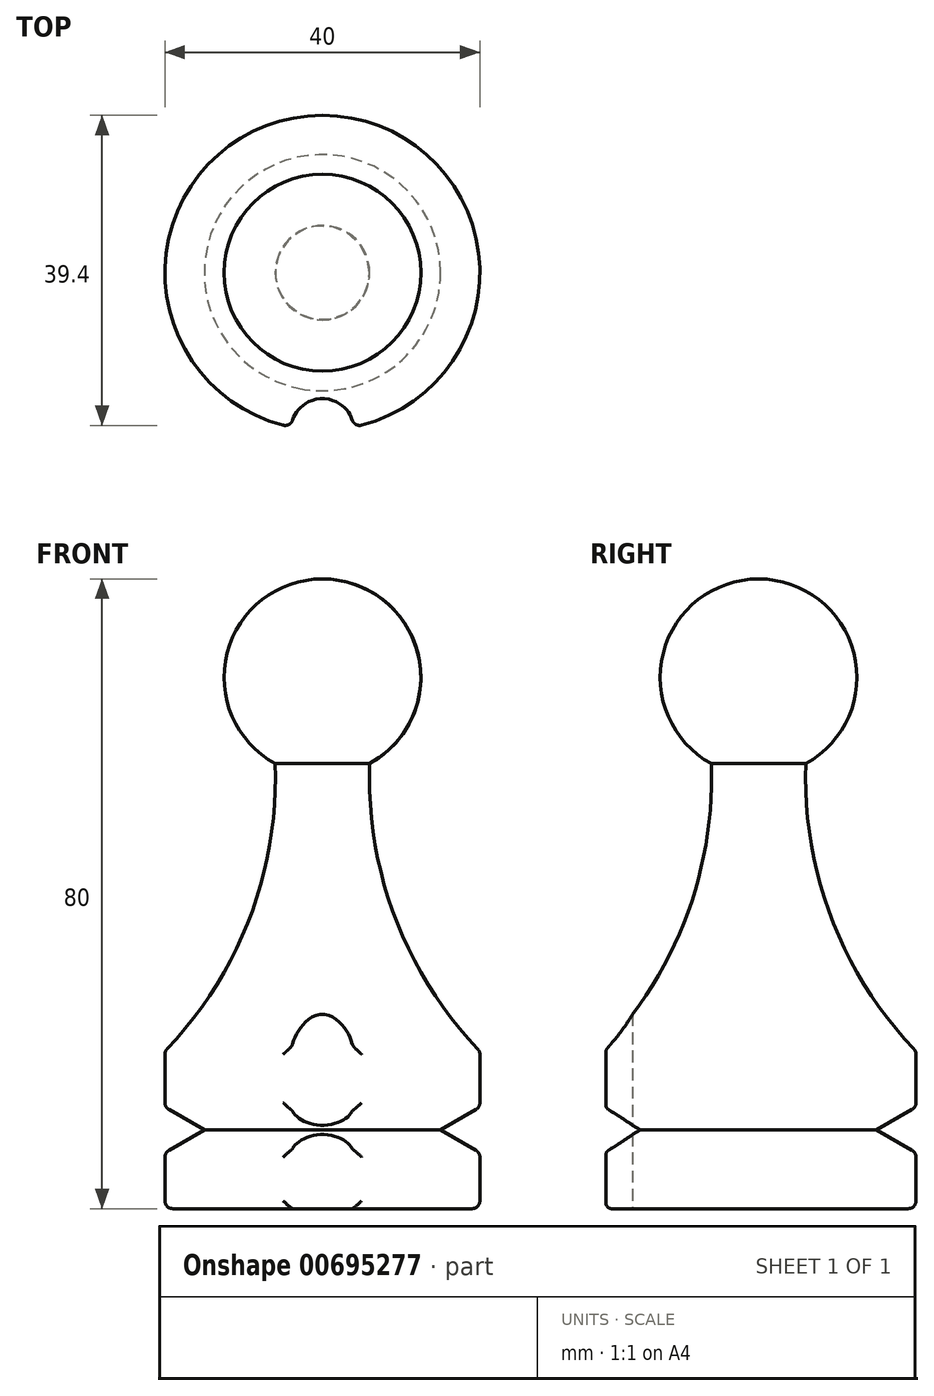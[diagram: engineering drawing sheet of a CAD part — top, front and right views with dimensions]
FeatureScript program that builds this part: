
annotation { "Feature Type Name" : "Feature", "Feature Type Description" : "" }
export const myFeature = defineFeature(function(context is Context, id is Id, definition is map)
    precondition{}
    {
        {
            var Q0;
            Q0=qCreatedBy(makeId("Front.planeOp"),FACE);
            var sketch = newSketch(context, id + "F0", { "sketchPlane" : qUnion([Q0])});
            skLineSegment(sketch, "E0", {"start": v(0, 87.13) * mm, "end": v(0, -76.3) * mm, "construction": true});
            skLineSegment(sketch, "E1", {"start": v(0, 0) * mm, "end": v(20, 0) * mm});
            skLineSegment(sketch, "E2", {"start": v(20, 0) * mm, "end": v(20, 7.11) * mm});
            skArc(sketch, "E3", {"start": v(6, 56.53) * mm, "mid": v(9.28, 36.84) * mm, "end": v(20, 20) * mm});
            skArc(sketch, "E4", {"start": v(6, 56.53) * mm, "mid": v(12.11, 70.6) * mm, "end": v(0, 80) * mm});
            skLineSegment(sketch, "E5", {"start": v(15, 10) * mm, "end": v(20, 7.11) * mm});
            skPoint(sketch, "E5.startSnap0", {"position": v(20, 10) * mm});
            skLineSegment(sketch, "E6", {"start": v(20, 7.11) * mm, "end": v(15, 10) * mm});
            skLineSegment(sketch, "E7", {"start": v(15, 10) * mm, "end": v(20, 12.89) * mm});
            skLineSegment(sketch, "E8.trimOffspring", {"start": v(20, 12.89) * mm, "end": v(20, 20) * mm});
            skLineSegment(sketch, "E9", {"start": v(0, 80) * mm, "end": v(0, 0) * mm});
            skSolve(sketch);
        }
        {
            var Q0;
            Q0 = qSketchRegion(id + "F0", true);
            var Q1;
            Q1=sQuery(id+"F0.wireOp",EDGE,"E0");
            revolve(context, id + "F1", {"entities" : qUnion([Q0]), "axis" : qUnion([Q1]), "revolveType" : RevolveType.FULL});
        }
        {
            var Q0;
            Q0=qCreatedBy(makeId("Top.planeOp"),FACE);
            var sketch = newSketch(context, id + "F2", { "sketchPlane" : qUnion([Q0])});
            skCircle(sketch, "E10.0", {"center": v(0, 0) * mm, "radius": 20 * mm});
            skCircle(sketch, "E11", {"center": v(0, -20) * mm, "radius": 4 * mm});
            skSolve(sketch);
        }
        {
            var Q0;
            {var subQ0=sQuery(id+"F2.wireOp",EDGE,"E11");var subQ1=sQuery(id+"F2.wireOp",EDGE,"E10.0");var subQ2=makeQuery(id+"F2.imprint","INTERSECT",VERTEX,{"disambiguationData":[OD(0.0)],"derivedFrom":[subQ1,subQ0]});Q0=makeQuery(id+"F2.imprint","IMPRINT",FACE,{"disambiguationData":[TD([[makeQuery(id+"F2.imprint","IMPRINT",EDGE,{"disambiguationData":[TD([[subQ2,-1.0]])],"derivedFrom":subQ1}),1.0]])]});}
            extrude(context, id + "F3", {"entities" : qUnion([Q0]), "operationType" : NewBodyOperationType.REMOVE, "depth" : 36.6 * mm, "offsetDistance" : 25 * mm});
        }
        {
            var Q0;
            {var subQ0=makeQuery(id+"F1.opRevolve","SWEPT_FACE",FACE,{"disambiguationData":[OSD([sQuery(id+"F0.wireOp",EDGE,"E3")])]});var subQ2=makeQuery(id+"F1.opRevolve","SWEPT_FACE",FACE,{"disambiguationData":[OSD([sQuery(id+"F0.wireOp",EDGE,"E8.trimOffspring")])]});var subQ3=sQuery(id+"F2.wireOp",EDGE,"E11");var subQ4=makeQuery(id+"F3.boolean.opBoolean","COPY",FACE,{"disambiguationData":[TD([subQ0])],"derivedFrom":makeQuery(id+"F3.opExtrude","SWEPT_FACE",FACE,{"disambiguationData":[OSD([subQ3])]})});Q0=makeQuery(id+"FiWPijupLubemqV_1.9.F3.boolean.opBoolean","SPLIT",FACE,{"disambiguationData":[TD([subQ4])],"derivedFrom":makeQuery(id+"FiWPijupLubemqV_1.8.F3.boolean.opBoolean","SPLIT",FACE,{"disambiguationData":[TD([subQ4])],"derivedFrom":makeQuery(id+"FiWPijupLubemqV_1.7.F3.boolean.opBoolean","SPLIT",FACE,{"disambiguationData":[TD([subQ4])],"derivedFrom":makeQuery(id+"FiWPijupLubemqV_1.6.F3.boolean.opBoolean","SPLIT",FACE,{"disambiguationData":[TD([subQ4])],"derivedFrom":makeQuery(id+"FiWPijupLubemqV_1.5.F3.boolean.opBoolean","SPLIT",FACE,{"disambiguationData":[TD([subQ4])],"derivedFrom":makeQuery(id+"FiWPijupLubemqV_1.4.F3.boolean.opBoolean","SPLIT",FACE,{"disambiguationData":[TD([subQ4])],"derivedFrom":makeQuery(id+"FiWPijupLubemqV_1.3.F3.boolean.opBoolean","SPLIT",FACE,{"disambiguationData":[TD([subQ4])],"derivedFrom":makeQuery(id+"FiWPijupLubemqV_1.2.F3.boolean.opBoolean","SPLIT",FACE,{"disambiguationData":[TD([subQ4])],"derivedFrom":makeQuery(id+"FiWPijupLubemqV_1.1.F3.boolean.opBoolean","SPLIT",FACE,{"disambiguationData":[OD(1.0)],"derivedFrom":subQ2})})})})})})})})});}
            var Q1;
            {var subQ0=makeQuery(id+"F1.opRevolve","SWEPT_FACE",FACE,{"disambiguationData":[OSD([sQuery(id+"F0.wireOp",EDGE,"E3")])]});var subQ2=makeQuery(id+"F1.opRevolve","SWEPT_FACE",FACE,{"disambiguationData":[OSD([sQuery(id+"F0.wireOp",EDGE,"E8.trimOffspring")])]});var subQ3=sQuery(id+"F2.wireOp",EDGE,"E11");var subQ4=makeQuery(id+"FiWPijupLubemqV_1.8.F3.opExtrude","SWEPT_FACE",FACE,{"disambiguationData":[OSD([subQ3])]});var subQ5=makeQuery(id+"F3.boolean.opBoolean","COPY",FACE,{"disambiguationData":[TD([subQ0])],"derivedFrom":makeQuery(id+"F3.opExtrude","SWEPT_FACE",FACE,{"disambiguationData":[OSD([subQ3])]})});Q1=makeQuery(id+"FiWPijupLubemqV_1.9.F3.boolean.opBoolean","SPLIT",FACE,{"disambiguationData":[TD([makeQuery(id+"FiWPijupLubemqV_1.8.F3.boolean.opBoolean","COPY",FACE,{"disambiguationData":[TD([subQ0])],"derivedFrom":subQ4})])],"derivedFrom":makeQuery(id+"FiWPijupLubemqV_1.8.F3.boolean.opBoolean","SPLIT",FACE,{"disambiguationData":[TD([subQ5])],"derivedFrom":makeQuery(id+"FiWPijupLubemqV_1.7.F3.boolean.opBoolean","SPLIT",FACE,{"disambiguationData":[TD([subQ5])],"derivedFrom":makeQuery(id+"FiWPijupLubemqV_1.6.F3.boolean.opBoolean","SPLIT",FACE,{"disambiguationData":[TD([subQ5])],"derivedFrom":makeQuery(id+"FiWPijupLubemqV_1.5.F3.boolean.opBoolean","SPLIT",FACE,{"disambiguationData":[TD([subQ5])],"derivedFrom":makeQuery(id+"FiWPijupLubemqV_1.4.F3.boolean.opBoolean","SPLIT",FACE,{"disambiguationData":[TD([subQ5])],"derivedFrom":makeQuery(id+"FiWPijupLubemqV_1.3.F3.boolean.opBoolean","SPLIT",FACE,{"disambiguationData":[TD([subQ5])],"derivedFrom":makeQuery(id+"FiWPijupLubemqV_1.2.F3.boolean.opBoolean","SPLIT",FACE,{"disambiguationData":[TD([subQ5])],"derivedFrom":makeQuery(id+"FiWPijupLubemqV_1.1.F3.boolean.opBoolean","SPLIT",FACE,{"disambiguationData":[OD(1.0)],"derivedFrom":subQ2})})})})})})})})});}
            var Q2;
            Q2=makeQuery(id+"FiWPijupLubemqV_1.1.F3.boolean.opBoolean","SPLIT",FACE,{"disambiguationData":[OD(0.0)],"derivedFrom":makeQuery(id+"F1.opRevolve","SWEPT_FACE",FACE,{"disambiguationData":[OSD([sQuery(id+"F0.wireOp",EDGE,"E8.trimOffspring")])]})});
            var Q3;
            {var subQ0=makeQuery(id+"F1.opRevolve","SWEPT_FACE",FACE,{"disambiguationData":[OSD([sQuery(id+"F0.wireOp",EDGE,"E3")])]});var subQ2=makeQuery(id+"F1.opRevolve","SWEPT_FACE",FACE,{"disambiguationData":[OSD([sQuery(id+"F0.wireOp",EDGE,"E8.trimOffspring")])]});var subQ3=sQuery(id+"F2.wireOp",EDGE,"E11");Q3=makeQuery(id+"FiWPijupLubemqV_1.2.F3.boolean.opBoolean","SPLIT",FACE,{"disambiguationData":[TD([makeQuery(id+"FiWPijupLubemqV_1.1.F3.boolean.opBoolean","COPY",FACE,{"disambiguationData":[TD([subQ0])],"derivedFrom":makeQuery(id+"FiWPijupLubemqV_1.1.F3.opExtrude","SWEPT_FACE",FACE,{"disambiguationData":[OSD([subQ3])]})})])],"derivedFrom":makeQuery(id+"FiWPijupLubemqV_1.1.F3.boolean.opBoolean","SPLIT",FACE,{"disambiguationData":[OD(1.0)],"derivedFrom":subQ2})});}
            var Q4;
            {var subQ0=makeQuery(id+"F1.opRevolve","SWEPT_FACE",FACE,{"disambiguationData":[OSD([sQuery(id+"F0.wireOp",EDGE,"E3")])]});var subQ2=makeQuery(id+"F1.opRevolve","SWEPT_FACE",FACE,{"disambiguationData":[OSD([sQuery(id+"F0.wireOp",EDGE,"E8.trimOffspring")])]});var subQ3=sQuery(id+"F2.wireOp",EDGE,"E11");var subQ4=makeQuery(id+"FiWPijupLubemqV_1.2.F3.opExtrude","SWEPT_FACE",FACE,{"disambiguationData":[OSD([subQ3])]});Q4=makeQuery(id+"FiWPijupLubemqV_1.3.F3.boolean.opBoolean","SPLIT",FACE,{"disambiguationData":[TD([makeQuery(id+"FiWPijupLubemqV_1.2.F3.boolean.opBoolean","COPY",FACE,{"disambiguationData":[TD([subQ0])],"derivedFrom":subQ4})])],"derivedFrom":makeQuery(id+"FiWPijupLubemqV_1.2.F3.boolean.opBoolean","SPLIT",FACE,{"disambiguationData":[TD([makeQuery(id+"F3.boolean.opBoolean","COPY",FACE,{"disambiguationData":[TD([subQ0])],"derivedFrom":makeQuery(id+"F3.opExtrude","SWEPT_FACE",FACE,{"disambiguationData":[OSD([subQ3])]})})])],"derivedFrom":makeQuery(id+"FiWPijupLubemqV_1.1.F3.boolean.opBoolean","SPLIT",FACE,{"disambiguationData":[OD(1.0)],"derivedFrom":subQ2})})});}
            var Q5;
            {var subQ0=makeQuery(id+"F1.opRevolve","SWEPT_FACE",FACE,{"disambiguationData":[OSD([sQuery(id+"F0.wireOp",EDGE,"E3")])]});var subQ2=makeQuery(id+"F1.opRevolve","SWEPT_FACE",FACE,{"disambiguationData":[OSD([sQuery(id+"F0.wireOp",EDGE,"E8.trimOffspring")])]});var subQ3=sQuery(id+"F2.wireOp",EDGE,"E11");var subQ4=makeQuery(id+"FiWPijupLubemqV_1.3.F3.opExtrude","SWEPT_FACE",FACE,{"disambiguationData":[OSD([subQ3])]});var subQ5=makeQuery(id+"F3.boolean.opBoolean","COPY",FACE,{"disambiguationData":[TD([subQ0])],"derivedFrom":makeQuery(id+"F3.opExtrude","SWEPT_FACE",FACE,{"disambiguationData":[OSD([subQ3])]})});Q5=makeQuery(id+"FiWPijupLubemqV_1.4.F3.boolean.opBoolean","SPLIT",FACE,{"disambiguationData":[TD([makeQuery(id+"FiWPijupLubemqV_1.3.F3.boolean.opBoolean","COPY",FACE,{"disambiguationData":[TD([subQ0])],"derivedFrom":subQ4})])],"derivedFrom":makeQuery(id+"FiWPijupLubemqV_1.3.F3.boolean.opBoolean","SPLIT",FACE,{"disambiguationData":[TD([subQ5])],"derivedFrom":makeQuery(id+"FiWPijupLubemqV_1.2.F3.boolean.opBoolean","SPLIT",FACE,{"disambiguationData":[TD([subQ5])],"derivedFrom":makeQuery(id+"FiWPijupLubemqV_1.1.F3.boolean.opBoolean","SPLIT",FACE,{"disambiguationData":[OD(1.0)],"derivedFrom":subQ2})})})});}
            var Q6;
            {var subQ0=makeQuery(id+"F1.opRevolve","SWEPT_FACE",FACE,{"disambiguationData":[OSD([sQuery(id+"F0.wireOp",EDGE,"E3")])]});var subQ2=makeQuery(id+"F1.opRevolve","SWEPT_FACE",FACE,{"disambiguationData":[OSD([sQuery(id+"F0.wireOp",EDGE,"E8.trimOffspring")])]});var subQ3=sQuery(id+"F2.wireOp",EDGE,"E11");var subQ4=makeQuery(id+"FiWPijupLubemqV_1.4.F3.opExtrude","SWEPT_FACE",FACE,{"disambiguationData":[OSD([subQ3])]});var subQ5=makeQuery(id+"F3.boolean.opBoolean","COPY",FACE,{"disambiguationData":[TD([subQ0])],"derivedFrom":makeQuery(id+"F3.opExtrude","SWEPT_FACE",FACE,{"disambiguationData":[OSD([subQ3])]})});Q6=makeQuery(id+"FiWPijupLubemqV_1.5.F3.boolean.opBoolean","SPLIT",FACE,{"disambiguationData":[TD([makeQuery(id+"FiWPijupLubemqV_1.4.F3.boolean.opBoolean","COPY",FACE,{"disambiguationData":[TD([subQ0])],"derivedFrom":subQ4})])],"derivedFrom":makeQuery(id+"FiWPijupLubemqV_1.4.F3.boolean.opBoolean","SPLIT",FACE,{"disambiguationData":[TD([subQ5])],"derivedFrom":makeQuery(id+"FiWPijupLubemqV_1.3.F3.boolean.opBoolean","SPLIT",FACE,{"disambiguationData":[TD([subQ5])],"derivedFrom":makeQuery(id+"FiWPijupLubemqV_1.2.F3.boolean.opBoolean","SPLIT",FACE,{"disambiguationData":[TD([subQ5])],"derivedFrom":makeQuery(id+"FiWPijupLubemqV_1.1.F3.boolean.opBoolean","SPLIT",FACE,{"disambiguationData":[OD(1.0)],"derivedFrom":subQ2})})})})});}
            var Q7;
            {var subQ0=makeQuery(id+"F1.opRevolve","SWEPT_FACE",FACE,{"disambiguationData":[OSD([sQuery(id+"F0.wireOp",EDGE,"E3")])]});var subQ2=makeQuery(id+"F1.opRevolve","SWEPT_FACE",FACE,{"disambiguationData":[OSD([sQuery(id+"F0.wireOp",EDGE,"E8.trimOffspring")])]});var subQ3=sQuery(id+"F2.wireOp",EDGE,"E11");var subQ4=makeQuery(id+"FiWPijupLubemqV_1.5.F3.opExtrude","SWEPT_FACE",FACE,{"disambiguationData":[OSD([subQ3])]});var subQ5=makeQuery(id+"F3.boolean.opBoolean","COPY",FACE,{"disambiguationData":[TD([subQ0])],"derivedFrom":makeQuery(id+"F3.opExtrude","SWEPT_FACE",FACE,{"disambiguationData":[OSD([subQ3])]})});Q7=makeQuery(id+"FiWPijupLubemqV_1.6.F3.boolean.opBoolean","SPLIT",FACE,{"disambiguationData":[TD([makeQuery(id+"FiWPijupLubemqV_1.5.F3.boolean.opBoolean","COPY",FACE,{"disambiguationData":[TD([subQ0])],"derivedFrom":subQ4})])],"derivedFrom":makeQuery(id+"FiWPijupLubemqV_1.5.F3.boolean.opBoolean","SPLIT",FACE,{"disambiguationData":[TD([subQ5])],"derivedFrom":makeQuery(id+"FiWPijupLubemqV_1.4.F3.boolean.opBoolean","SPLIT",FACE,{"disambiguationData":[TD([subQ5])],"derivedFrom":makeQuery(id+"FiWPijupLubemqV_1.3.F3.boolean.opBoolean","SPLIT",FACE,{"disambiguationData":[TD([subQ5])],"derivedFrom":makeQuery(id+"FiWPijupLubemqV_1.2.F3.boolean.opBoolean","SPLIT",FACE,{"disambiguationData":[TD([subQ5])],"derivedFrom":makeQuery(id+"FiWPijupLubemqV_1.1.F3.boolean.opBoolean","SPLIT",FACE,{"disambiguationData":[OD(1.0)],"derivedFrom":subQ2})})})})})});}
            var Q8;
            {var subQ0=makeQuery(id+"F1.opRevolve","SWEPT_FACE",FACE,{"disambiguationData":[OSD([sQuery(id+"F0.wireOp",EDGE,"E3")])]});var subQ2=makeQuery(id+"F1.opRevolve","SWEPT_FACE",FACE,{"disambiguationData":[OSD([sQuery(id+"F0.wireOp",EDGE,"E8.trimOffspring")])]});var subQ3=sQuery(id+"F2.wireOp",EDGE,"E11");var subQ4=makeQuery(id+"FiWPijupLubemqV_1.7.F3.opExtrude","SWEPT_FACE",FACE,{"disambiguationData":[OSD([subQ3])]});var subQ5=makeQuery(id+"F3.boolean.opBoolean","COPY",FACE,{"disambiguationData":[TD([subQ0])],"derivedFrom":makeQuery(id+"F3.opExtrude","SWEPT_FACE",FACE,{"disambiguationData":[OSD([subQ3])]})});Q8=makeQuery(id+"FiWPijupLubemqV_1.8.F3.boolean.opBoolean","SPLIT",FACE,{"disambiguationData":[TD([makeQuery(id+"FiWPijupLubemqV_1.7.F3.boolean.opBoolean","COPY",FACE,{"disambiguationData":[TD([subQ0])],"derivedFrom":subQ4})])],"derivedFrom":makeQuery(id+"FiWPijupLubemqV_1.7.F3.boolean.opBoolean","SPLIT",FACE,{"disambiguationData":[TD([subQ5])],"derivedFrom":makeQuery(id+"FiWPijupLubemqV_1.6.F3.boolean.opBoolean","SPLIT",FACE,{"disambiguationData":[TD([subQ5])],"derivedFrom":makeQuery(id+"FiWPijupLubemqV_1.5.F3.boolean.opBoolean","SPLIT",FACE,{"disambiguationData":[TD([subQ5])],"derivedFrom":makeQuery(id+"FiWPijupLubemqV_1.4.F3.boolean.opBoolean","SPLIT",FACE,{"disambiguationData":[TD([subQ5])],"derivedFrom":makeQuery(id+"FiWPijupLubemqV_1.3.F3.boolean.opBoolean","SPLIT",FACE,{"disambiguationData":[TD([subQ5])],"derivedFrom":makeQuery(id+"FiWPijupLubemqV_1.2.F3.boolean.opBoolean","SPLIT",FACE,{"disambiguationData":[TD([subQ5])],"derivedFrom":makeQuery(id+"FiWPijupLubemqV_1.1.F3.boolean.opBoolean","SPLIT",FACE,{"disambiguationData":[OD(1.0)],"derivedFrom":subQ2})})})})})})})});}
            var Q9;
            {var subQ0=makeQuery(id+"F1.opRevolve","SWEPT_FACE",FACE,{"disambiguationData":[OSD([sQuery(id+"F0.wireOp",EDGE,"E3")])]});var subQ2=makeQuery(id+"F1.opRevolve","SWEPT_FACE",FACE,{"disambiguationData":[OSD([sQuery(id+"F0.wireOp",EDGE,"E8.trimOffspring")])]});var subQ3=sQuery(id+"F2.wireOp",EDGE,"E11");var subQ4=makeQuery(id+"FiWPijupLubemqV_1.6.F3.opExtrude","SWEPT_FACE",FACE,{"disambiguationData":[OSD([subQ3])]});var subQ5=makeQuery(id+"F3.boolean.opBoolean","COPY",FACE,{"disambiguationData":[TD([subQ0])],"derivedFrom":makeQuery(id+"F3.opExtrude","SWEPT_FACE",FACE,{"disambiguationData":[OSD([subQ3])]})});Q9=makeQuery(id+"FiWPijupLubemqV_1.7.F3.boolean.opBoolean","SPLIT",FACE,{"disambiguationData":[TD([makeQuery(id+"FiWPijupLubemqV_1.6.F3.boolean.opBoolean","COPY",FACE,{"disambiguationData":[TD([subQ0])],"derivedFrom":subQ4})])],"derivedFrom":makeQuery(id+"FiWPijupLubemqV_1.6.F3.boolean.opBoolean","SPLIT",FACE,{"disambiguationData":[TD([subQ5])],"derivedFrom":makeQuery(id+"FiWPijupLubemqV_1.5.F3.boolean.opBoolean","SPLIT",FACE,{"disambiguationData":[TD([subQ5])],"derivedFrom":makeQuery(id+"FiWPijupLubemqV_1.4.F3.boolean.opBoolean","SPLIT",FACE,{"disambiguationData":[TD([subQ5])],"derivedFrom":makeQuery(id+"FiWPijupLubemqV_1.3.F3.boolean.opBoolean","SPLIT",FACE,{"disambiguationData":[TD([subQ5])],"derivedFrom":makeQuery(id+"FiWPijupLubemqV_1.2.F3.boolean.opBoolean","SPLIT",FACE,{"disambiguationData":[TD([subQ5])],"derivedFrom":makeQuery(id+"FiWPijupLubemqV_1.1.F3.boolean.opBoolean","SPLIT",FACE,{"disambiguationData":[OD(1.0)],"derivedFrom":subQ2})})})})})})});}
            var Q10;
            {var subQ0=makeQuery(id+"F1.opRevolve","SWEPT_FACE",FACE,{"disambiguationData":[OSD([sQuery(id+"F0.wireOp",EDGE,"E1")])]});var subQ2=makeQuery(id+"F1.opRevolve","SWEPT_FACE",FACE,{"disambiguationData":[OSD([sQuery(id+"F0.wireOp",EDGE,"E2")])]});var subQ3=sQuery(id+"F2.wireOp",EDGE,"E11");var subQ4=makeQuery(id+"FiWPijupLubemqV_1.7.F3.opExtrude","SWEPT_FACE",FACE,{"disambiguationData":[OSD([subQ3])]});var subQ5=makeQuery(id+"F3.boolean.opBoolean","COPY",FACE,{"disambiguationData":[TD([subQ0])],"derivedFrom":makeQuery(id+"F3.opExtrude","SWEPT_FACE",FACE,{"disambiguationData":[OSD([subQ3])]})});Q10=makeQuery(id+"FiWPijupLubemqV_1.8.F3.boolean.opBoolean","SPLIT",FACE,{"disambiguationData":[TD([makeQuery(id+"FiWPijupLubemqV_1.7.F3.boolean.opBoolean","COPY",FACE,{"disambiguationData":[TD([subQ0])],"derivedFrom":subQ4})])],"derivedFrom":makeQuery(id+"FiWPijupLubemqV_1.7.F3.boolean.opBoolean","SPLIT",FACE,{"disambiguationData":[TD([subQ5])],"derivedFrom":makeQuery(id+"FiWPijupLubemqV_1.6.F3.boolean.opBoolean","SPLIT",FACE,{"disambiguationData":[TD([subQ5])],"derivedFrom":makeQuery(id+"FiWPijupLubemqV_1.5.F3.boolean.opBoolean","SPLIT",FACE,{"disambiguationData":[TD([subQ5])],"derivedFrom":makeQuery(id+"FiWPijupLubemqV_1.4.F3.boolean.opBoolean","SPLIT",FACE,{"disambiguationData":[TD([subQ5])],"derivedFrom":makeQuery(id+"FiWPijupLubemqV_1.3.F3.boolean.opBoolean","SPLIT",FACE,{"disambiguationData":[TD([subQ5])],"derivedFrom":makeQuery(id+"FiWPijupLubemqV_1.2.F3.boolean.opBoolean","SPLIT",FACE,{"disambiguationData":[TD([subQ5])],"derivedFrom":makeQuery(id+"FiWPijupLubemqV_1.1.F3.boolean.opBoolean","SPLIT",FACE,{"disambiguationData":[OD(1.0)],"derivedFrom":subQ2})})})})})})})});}
            var Q11;
            {var subQ0=makeQuery(id+"F1.opRevolve","SWEPT_FACE",FACE,{"disambiguationData":[OSD([sQuery(id+"F0.wireOp",EDGE,"E1")])]});var subQ1=sQuery(id+"F2.wireOp",EDGE,"E11");var subQ3=makeQuery(id+"F1.opRevolve","SWEPT_FACE",FACE,{"disambiguationData":[OSD([sQuery(id+"F0.wireOp",EDGE,"E2")])]});var subQ4=makeQuery(id+"FiWPijupLubemqV_1.6.F3.opExtrude","SWEPT_FACE",FACE,{"disambiguationData":[OSD([subQ1])]});var subQ5=makeQuery(id+"F3.boolean.opBoolean","COPY",FACE,{"disambiguationData":[TD([subQ0])],"derivedFrom":makeQuery(id+"F3.opExtrude","SWEPT_FACE",FACE,{"disambiguationData":[OSD([subQ1])]})});Q11=makeQuery(id+"FiWPijupLubemqV_1.7.F3.boolean.opBoolean","SPLIT",FACE,{"disambiguationData":[TD([makeQuery(id+"FiWPijupLubemqV_1.6.F3.boolean.opBoolean","COPY",FACE,{"disambiguationData":[TD([subQ0])],"derivedFrom":subQ4})])],"derivedFrom":makeQuery(id+"FiWPijupLubemqV_1.6.F3.boolean.opBoolean","SPLIT",FACE,{"disambiguationData":[TD([subQ5])],"derivedFrom":makeQuery(id+"FiWPijupLubemqV_1.5.F3.boolean.opBoolean","SPLIT",FACE,{"disambiguationData":[TD([subQ5])],"derivedFrom":makeQuery(id+"FiWPijupLubemqV_1.4.F3.boolean.opBoolean","SPLIT",FACE,{"disambiguationData":[TD([subQ5])],"derivedFrom":makeQuery(id+"FiWPijupLubemqV_1.3.F3.boolean.opBoolean","SPLIT",FACE,{"disambiguationData":[TD([subQ5])],"derivedFrom":makeQuery(id+"FiWPijupLubemqV_1.2.F3.boolean.opBoolean","SPLIT",FACE,{"disambiguationData":[TD([subQ5])],"derivedFrom":makeQuery(id+"FiWPijupLubemqV_1.1.F3.boolean.opBoolean","SPLIT",FACE,{"disambiguationData":[OD(1.0)],"derivedFrom":subQ3})})})})})})});}
            var Q12;
            {var subQ0=makeQuery(id+"F1.opRevolve","SWEPT_FACE",FACE,{"disambiguationData":[OSD([sQuery(id+"F0.wireOp",EDGE,"E1")])]});var subQ2=makeQuery(id+"F1.opRevolve","SWEPT_FACE",FACE,{"disambiguationData":[OSD([sQuery(id+"F0.wireOp",EDGE,"E2")])]});var subQ3=sQuery(id+"F2.wireOp",EDGE,"E11");var subQ4=makeQuery(id+"FiWPijupLubemqV_1.5.F3.opExtrude","SWEPT_FACE",FACE,{"disambiguationData":[OSD([subQ3])]});var subQ5=makeQuery(id+"F3.boolean.opBoolean","COPY",FACE,{"disambiguationData":[TD([subQ0])],"derivedFrom":makeQuery(id+"F3.opExtrude","SWEPT_FACE",FACE,{"disambiguationData":[OSD([subQ3])]})});Q12=makeQuery(id+"FiWPijupLubemqV_1.6.F3.boolean.opBoolean","SPLIT",FACE,{"disambiguationData":[TD([makeQuery(id+"FiWPijupLubemqV_1.5.F3.boolean.opBoolean","COPY",FACE,{"disambiguationData":[TD([subQ0])],"derivedFrom":subQ4})])],"derivedFrom":makeQuery(id+"FiWPijupLubemqV_1.5.F3.boolean.opBoolean","SPLIT",FACE,{"disambiguationData":[TD([subQ5])],"derivedFrom":makeQuery(id+"FiWPijupLubemqV_1.4.F3.boolean.opBoolean","SPLIT",FACE,{"disambiguationData":[TD([subQ5])],"derivedFrom":makeQuery(id+"FiWPijupLubemqV_1.3.F3.boolean.opBoolean","SPLIT",FACE,{"disambiguationData":[TD([subQ5])],"derivedFrom":makeQuery(id+"FiWPijupLubemqV_1.2.F3.boolean.opBoolean","SPLIT",FACE,{"disambiguationData":[TD([subQ5])],"derivedFrom":makeQuery(id+"FiWPijupLubemqV_1.1.F3.boolean.opBoolean","SPLIT",FACE,{"disambiguationData":[OD(1.0)],"derivedFrom":subQ2})})})})})});}
            var Q13;
            {var subQ0=makeQuery(id+"F1.opRevolve","SWEPT_FACE",FACE,{"disambiguationData":[OSD([sQuery(id+"F0.wireOp",EDGE,"E1")])]});var subQ1=makeQuery(id+"F1.opRevolve","SWEPT_FACE",FACE,{"disambiguationData":[OSD([sQuery(id+"F0.wireOp",EDGE,"E2")])]});var subQ3=sQuery(id+"F2.wireOp",EDGE,"E11");var subQ4=makeQuery(id+"FiWPijupLubemqV_1.4.F3.opExtrude","SWEPT_FACE",FACE,{"disambiguationData":[OSD([subQ3])]});var subQ5=makeQuery(id+"F3.boolean.opBoolean","COPY",FACE,{"disambiguationData":[TD([subQ0])],"derivedFrom":makeQuery(id+"F3.opExtrude","SWEPT_FACE",FACE,{"disambiguationData":[OSD([subQ3])]})});Q13=makeQuery(id+"FiWPijupLubemqV_1.5.F3.boolean.opBoolean","SPLIT",FACE,{"disambiguationData":[TD([makeQuery(id+"FiWPijupLubemqV_1.4.F3.boolean.opBoolean","COPY",FACE,{"disambiguationData":[TD([subQ0])],"derivedFrom":subQ4})])],"derivedFrom":makeQuery(id+"FiWPijupLubemqV_1.4.F3.boolean.opBoolean","SPLIT",FACE,{"disambiguationData":[TD([subQ5])],"derivedFrom":makeQuery(id+"FiWPijupLubemqV_1.3.F3.boolean.opBoolean","SPLIT",FACE,{"disambiguationData":[TD([subQ5])],"derivedFrom":makeQuery(id+"FiWPijupLubemqV_1.2.F3.boolean.opBoolean","SPLIT",FACE,{"disambiguationData":[TD([subQ5])],"derivedFrom":makeQuery(id+"FiWPijupLubemqV_1.1.F3.boolean.opBoolean","SPLIT",FACE,{"disambiguationData":[OD(1.0)],"derivedFrom":subQ1})})})})});}
            var Q14;
            {var subQ0=makeQuery(id+"F1.opRevolve","SWEPT_FACE",FACE,{"disambiguationData":[OSD([sQuery(id+"F0.wireOp",EDGE,"E1")])]});var subQ2=sQuery(id+"F2.wireOp",EDGE,"E11");var subQ3=makeQuery(id+"F1.opRevolve","SWEPT_FACE",FACE,{"disambiguationData":[OSD([sQuery(id+"F0.wireOp",EDGE,"E2")])]});var subQ4=makeQuery(id+"FiWPijupLubemqV_1.3.F3.opExtrude","SWEPT_FACE",FACE,{"disambiguationData":[OSD([subQ2])]});var subQ5=makeQuery(id+"F3.boolean.opBoolean","COPY",FACE,{"disambiguationData":[TD([subQ0])],"derivedFrom":makeQuery(id+"F3.opExtrude","SWEPT_FACE",FACE,{"disambiguationData":[OSD([subQ2])]})});Q14=makeQuery(id+"FiWPijupLubemqV_1.4.F3.boolean.opBoolean","SPLIT",FACE,{"disambiguationData":[TD([makeQuery(id+"FiWPijupLubemqV_1.3.F3.boolean.opBoolean","COPY",FACE,{"disambiguationData":[TD([subQ0])],"derivedFrom":subQ4})])],"derivedFrom":makeQuery(id+"FiWPijupLubemqV_1.3.F3.boolean.opBoolean","SPLIT",FACE,{"disambiguationData":[TD([subQ5])],"derivedFrom":makeQuery(id+"FiWPijupLubemqV_1.2.F3.boolean.opBoolean","SPLIT",FACE,{"disambiguationData":[TD([subQ5])],"derivedFrom":makeQuery(id+"FiWPijupLubemqV_1.1.F3.boolean.opBoolean","SPLIT",FACE,{"disambiguationData":[OD(1.0)],"derivedFrom":subQ3})})})});}
            var Q15;
            {var subQ0=makeQuery(id+"F1.opRevolve","SWEPT_FACE",FACE,{"disambiguationData":[OSD([sQuery(id+"F0.wireOp",EDGE,"E1")])]});var subQ2=makeQuery(id+"F1.opRevolve","SWEPT_FACE",FACE,{"disambiguationData":[OSD([sQuery(id+"F0.wireOp",EDGE,"E2")])]});var subQ3=sQuery(id+"F2.wireOp",EDGE,"E11");var subQ4=makeQuery(id+"FiWPijupLubemqV_1.2.F3.opExtrude","SWEPT_FACE",FACE,{"disambiguationData":[OSD([subQ3])]});Q15=makeQuery(id+"FiWPijupLubemqV_1.3.F3.boolean.opBoolean","SPLIT",FACE,{"disambiguationData":[TD([makeQuery(id+"FiWPijupLubemqV_1.2.F3.boolean.opBoolean","COPY",FACE,{"disambiguationData":[TD([subQ0])],"derivedFrom":subQ4})])],"derivedFrom":makeQuery(id+"FiWPijupLubemqV_1.2.F3.boolean.opBoolean","SPLIT",FACE,{"disambiguationData":[TD([makeQuery(id+"F3.boolean.opBoolean","COPY",FACE,{"disambiguationData":[TD([subQ0])],"derivedFrom":makeQuery(id+"F3.opExtrude","SWEPT_FACE",FACE,{"disambiguationData":[OSD([subQ3])]})})])],"derivedFrom":makeQuery(id+"FiWPijupLubemqV_1.1.F3.boolean.opBoolean","SPLIT",FACE,{"disambiguationData":[OD(1.0)],"derivedFrom":subQ2})})});}
            var Q16;
            {var subQ0=makeQuery(id+"F1.opRevolve","SWEPT_FACE",FACE,{"disambiguationData":[OSD([sQuery(id+"F0.wireOp",EDGE,"E1")])]});var subQ1=sQuery(id+"F2.wireOp",EDGE,"E11");var subQ3=makeQuery(id+"F1.opRevolve","SWEPT_FACE",FACE,{"disambiguationData":[OSD([sQuery(id+"F0.wireOp",EDGE,"E2")])]});Q16=makeQuery(id+"FiWPijupLubemqV_1.2.F3.boolean.opBoolean","SPLIT",FACE,{"disambiguationData":[TD([makeQuery(id+"FiWPijupLubemqV_1.1.F3.boolean.opBoolean","COPY",FACE,{"disambiguationData":[TD([subQ0])],"derivedFrom":makeQuery(id+"FiWPijupLubemqV_1.1.F3.opExtrude","SWEPT_FACE",FACE,{"disambiguationData":[OSD([subQ1])]})})])],"derivedFrom":makeQuery(id+"FiWPijupLubemqV_1.1.F3.boolean.opBoolean","SPLIT",FACE,{"disambiguationData":[OD(1.0)],"derivedFrom":subQ3})});}
            var Q17;
            Q17=makeQuery(id+"FiWPijupLubemqV_1.1.F3.boolean.opBoolean","SPLIT",FACE,{"disambiguationData":[OD(0.0)],"derivedFrom":makeQuery(id+"F1.opRevolve","SWEPT_FACE",FACE,{"disambiguationData":[OSD([sQuery(id+"F0.wireOp",EDGE,"E2")])]})});
            var Q18;
            {var subQ0=makeQuery(id+"F1.opRevolve","SWEPT_FACE",FACE,{"disambiguationData":[OSD([sQuery(id+"F0.wireOp",EDGE,"E1")])]});var subQ1=makeQuery(id+"F1.opRevolve","SWEPT_FACE",FACE,{"disambiguationData":[OSD([sQuery(id+"F0.wireOp",EDGE,"E2")])]});var subQ3=sQuery(id+"F2.wireOp",EDGE,"E11");var subQ4=makeQuery(id+"F3.boolean.opBoolean","COPY",FACE,{"disambiguationData":[TD([subQ0])],"derivedFrom":makeQuery(id+"F3.opExtrude","SWEPT_FACE",FACE,{"disambiguationData":[OSD([subQ3])]})});Q18=makeQuery(id+"FiWPijupLubemqV_1.9.F3.boolean.opBoolean","SPLIT",FACE,{"disambiguationData":[TD([subQ4])],"derivedFrom":makeQuery(id+"FiWPijupLubemqV_1.8.F3.boolean.opBoolean","SPLIT",FACE,{"disambiguationData":[TD([subQ4])],"derivedFrom":makeQuery(id+"FiWPijupLubemqV_1.7.F3.boolean.opBoolean","SPLIT",FACE,{"disambiguationData":[TD([subQ4])],"derivedFrom":makeQuery(id+"FiWPijupLubemqV_1.6.F3.boolean.opBoolean","SPLIT",FACE,{"disambiguationData":[TD([subQ4])],"derivedFrom":makeQuery(id+"FiWPijupLubemqV_1.5.F3.boolean.opBoolean","SPLIT",FACE,{"disambiguationData":[TD([subQ4])],"derivedFrom":makeQuery(id+"FiWPijupLubemqV_1.4.F3.boolean.opBoolean","SPLIT",FACE,{"disambiguationData":[TD([subQ4])],"derivedFrom":makeQuery(id+"FiWPijupLubemqV_1.3.F3.boolean.opBoolean","SPLIT",FACE,{"disambiguationData":[TD([subQ4])],"derivedFrom":makeQuery(id+"FiWPijupLubemqV_1.2.F3.boolean.opBoolean","SPLIT",FACE,{"disambiguationData":[TD([subQ4])],"derivedFrom":makeQuery(id+"FiWPijupLubemqV_1.1.F3.boolean.opBoolean","SPLIT",FACE,{"disambiguationData":[OD(1.0)],"derivedFrom":subQ1})})})})})})})})});}
            var Q19;
            {var subQ0=makeQuery(id+"F1.opRevolve","SWEPT_FACE",FACE,{"disambiguationData":[OSD([sQuery(id+"F0.wireOp",EDGE,"E1")])]});var subQ2=sQuery(id+"F2.wireOp",EDGE,"E11");var subQ3=makeQuery(id+"F1.opRevolve","SWEPT_FACE",FACE,{"disambiguationData":[OSD([sQuery(id+"F0.wireOp",EDGE,"E2")])]});var subQ4=makeQuery(id+"FiWPijupLubemqV_1.8.F3.opExtrude","SWEPT_FACE",FACE,{"disambiguationData":[OSD([subQ2])]});var subQ5=makeQuery(id+"F3.boolean.opBoolean","COPY",FACE,{"disambiguationData":[TD([subQ0])],"derivedFrom":makeQuery(id+"F3.opExtrude","SWEPT_FACE",FACE,{"disambiguationData":[OSD([subQ2])]})});Q19=makeQuery(id+"FiWPijupLubemqV_1.9.F3.boolean.opBoolean","SPLIT",FACE,{"disambiguationData":[TD([makeQuery(id+"FiWPijupLubemqV_1.8.F3.boolean.opBoolean","COPY",FACE,{"disambiguationData":[TD([subQ0])],"derivedFrom":subQ4})])],"derivedFrom":makeQuery(id+"FiWPijupLubemqV_1.8.F3.boolean.opBoolean","SPLIT",FACE,{"disambiguationData":[TD([subQ5])],"derivedFrom":makeQuery(id+"FiWPijupLubemqV_1.7.F3.boolean.opBoolean","SPLIT",FACE,{"disambiguationData":[TD([subQ5])],"derivedFrom":makeQuery(id+"FiWPijupLubemqV_1.6.F3.boolean.opBoolean","SPLIT",FACE,{"disambiguationData":[TD([subQ5])],"derivedFrom":makeQuery(id+"FiWPijupLubemqV_1.5.F3.boolean.opBoolean","SPLIT",FACE,{"disambiguationData":[TD([subQ5])],"derivedFrom":makeQuery(id+"FiWPijupLubemqV_1.4.F3.boolean.opBoolean","SPLIT",FACE,{"disambiguationData":[TD([subQ5])],"derivedFrom":makeQuery(id+"FiWPijupLubemqV_1.3.F3.boolean.opBoolean","SPLIT",FACE,{"disambiguationData":[TD([subQ5])],"derivedFrom":makeQuery(id+"FiWPijupLubemqV_1.2.F3.boolean.opBoolean","SPLIT",FACE,{"disambiguationData":[TD([subQ5])],"derivedFrom":makeQuery(id+"FiWPijupLubemqV_1.1.F3.boolean.opBoolean","SPLIT",FACE,{"disambiguationData":[OD(1.0)],"derivedFrom":subQ3})})})})})})})})});}
            fillet(context, id + "F4", {"entities" : qUnion([Q0, Q1, Q2, Q3, Q4, Q5, Q6, Q7, Q8, Q9, Q10, Q11, Q12, Q13, Q14, Q15, Q16, Q17, Q18, Q19]), "radius" : 1 * mm, "tangentPropagation" : true, "allowEdgeOverflow" : false});
        }
    });
